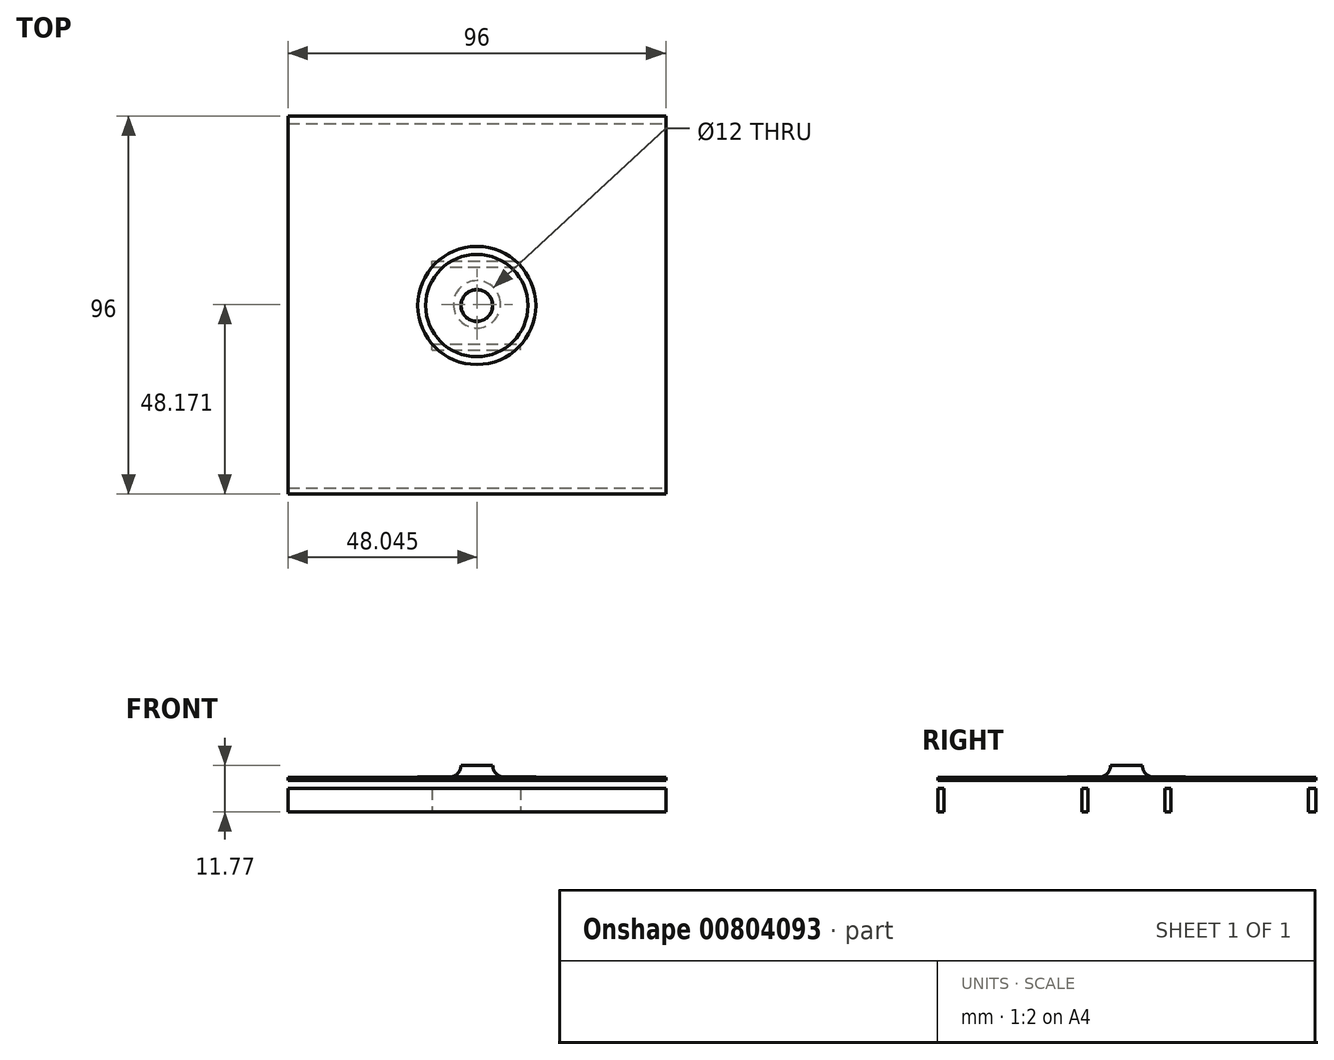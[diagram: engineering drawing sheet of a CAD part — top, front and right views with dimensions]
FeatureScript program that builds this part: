
annotation { "Feature Type Name" : "Feature", "Feature Type Description" : "" }
export const myFeature = defineFeature(function(context is Context, id is Id, definition is map)
    precondition{}
    {
        {
            var Q0;
            Q0=qCreatedBy(makeId("Top.planeOp"),FACE);
            var sketch = newSketch(context, id + "F0", { "sketchPlane" : qUnion([Q0])});
            skLineSegment(sketch, "E0.bottom", {"start": v(-47.87, 48.13) * mm, "end": v(48.13, 48.13) * mm});
            skLineSegment(sketch, "E0.top", {"start": v(-47.87, 46.17) * mm, "end": v(48.13, 46.17) * mm});
            skLineSegment(sketch, "E0.left", {"start": v(-47.87, 48.13) * mm, "end": v(-47.87, 46.17) * mm});
            skLineSegment(sketch, "E0.right", {"start": v(48.13, 48.13) * mm, "end": v(48.13, 46.17) * mm});
            skLineSegment(sketch, "E1.bottom", {"start": v(-47.87, 46.17) * mm, "end": v(-46.43, 46.17) * mm});
            skLineSegment(sketch, "E1.top", {"start": v(-47.87, -46.37) * mm, "end": v(-46.43, -46.37) * mm});
            skLineSegment(sketch, "E1.left", {"start": v(-47.87, 46.17) * mm, "end": v(-47.87, -46.37) * mm});
            skLineSegment(sketch, "E1.right", {"start": v(-46.43, 46.17) * mm, "end": v(-46.43, -46.37) * mm});
            skLineSegment(sketch, "E2.bottom", {"start": v(-47.87, -46.37) * mm, "end": v(48.13, -46.37) * mm});
            skLineSegment(sketch, "E2.top", {"start": v(-47.87, -47.87) * mm, "end": v(48.13, -47.87) * mm});
            skLineSegment(sketch, "E2.left", {"start": v(-47.87, -46.37) * mm, "end": v(-47.87, -47.87) * mm});
            skLineSegment(sketch, "E2.right", {"start": v(48.13, -46.37) * mm, "end": v(48.13, -47.87) * mm});
            skLineSegment(sketch, "E3.bottom", {"start": v(48.13, 46.17) * mm, "end": v(46.57, 46.17) * mm});
            skLineSegment(sketch, "E3.top", {"start": v(48.13, -46.37) * mm, "end": v(46.57, -46.37) * mm});
            skLineSegment(sketch, "E3.left", {"start": v(48.13, 46.17) * mm, "end": v(48.13, -46.37) * mm});
            skLineSegment(sketch, "E3.right", {"start": v(46.57, 46.17) * mm, "end": v(46.57, -46.37) * mm});
            skLineSegment(sketch, "E4.bottom", {"start": v(-11.25, -11.25) * mm, "end": v(11.25, -11.25) * mm});
            skLineSegment(sketch, "E4.top", {"start": v(-11.25, 11.25) * mm, "end": v(11.25, 11.25) * mm});
            skLineSegment(sketch, "E4.left", {"start": v(-11.25, -11.25) * mm, "end": v(-11.25, 11.25) * mm});
            skLineSegment(sketch, "E4.right", {"start": v(11.25, -11.25) * mm, "end": v(11.25, 11.25) * mm});
            skPoint(sketch, "E4.middle", {"position": v(0, 0) * mm});
            skLineSegment(sketch, "E5.bottom", {"start": v(-11.25, 46.17) * mm, "end": v(-12.75, 46.17) * mm});
            skLineSegment(sketch, "E5.top", {"start": v(-11.25, -46.37) * mm, "end": v(-12.75, -46.37) * mm});
            skLineSegment(sketch, "E5.left", {"start": v(-11.25, 46.17) * mm, "end": v(-11.25, -46.37) * mm});
            skLineSegment(sketch, "E5.right", {"start": v(-12.75, 46.17) * mm, "end": v(-12.75, -46.37) * mm});
            skLineSegment(sketch, "E6.bottom", {"start": v(-0.75, 11.25) * mm, "end": v(0.75, 11.25) * mm});
            skLineSegment(sketch, "E6.top", {"start": v(-0.75, 46.17) * mm, "end": v(0.75, 46.17) * mm});
            skLineSegment(sketch, "E6.left", {"start": v(-0.75, 11.25) * mm, "end": v(-0.75, 46.17) * mm});
            skLineSegment(sketch, "E6.right", {"start": v(0.75, 11.25) * mm, "end": v(0.75, 46.17) * mm});
            skLineSegment(sketch, "E7", {"start": v(0, 0) * mm, "end": v(0, 0) * mm, "construction": true});
            skLineSegment(sketch, "E8.top", {"start": v(-11.25, 9.75) * mm, "end": v(11.25, 9.75) * mm});
            skLineSegment(sketch, "E8.left", {"start": v(-11.25, 11.25) * mm, "end": v(-11.25, 9.75) * mm});
            skLineSegment(sketch, "E8.right", {"start": v(11.25, 11.25) * mm, "end": v(11.25, 9.75) * mm});
            skLineSegment(sketch, "E9.top", {"start": v(-11.25, -9.75) * mm, "end": v(11.25, -9.75) * mm});
            skLineSegment(sketch, "E9.left", {"start": v(-11.25, -11.25) * mm, "end": v(-11.25, -9.75) * mm});
            skLineSegment(sketch, "E9.right", {"start": v(11.25, -11.25) * mm, "end": v(11.25, -9.75) * mm});
            skLineSegment(sketch, "E10.bottom", {"start": v(-0.77, -11.25) * mm, "end": v(0.73, -11.25) * mm});
            skLineSegment(sketch, "E10.top", {"start": v(-0.77, -46.37) * mm, "end": v(0.73, -46.37) * mm});
            skLineSegment(sketch, "E10.left", {"start": v(-0.77, -11.25) * mm, "end": v(-0.77, -46.37) * mm});
            skLineSegment(sketch, "E10.right", {"start": v(0.73, -11.25) * mm, "end": v(0.73, -46.37) * mm});
            skLineSegment(sketch, "E11.bottom", {"start": v(11.25, -46.37) * mm, "end": v(12.75, -46.37) * mm});
            skLineSegment(sketch, "E11.top", {"start": v(11.25, 46.17) * mm, "end": v(12.75, 46.17) * mm});
            skLineSegment(sketch, "E11.left", {"start": v(11.25, -46.37) * mm, "end": v(11.25, 46.17) * mm});
            skLineSegment(sketch, "E11.right", {"start": v(12.75, -46.37) * mm, "end": v(12.75, 46.17) * mm});
            skLineSegment(sketch, "E12.bottom", {"start": v(-22.73, -46.37) * mm, "end": v(-24.23, -46.37) * mm});
            skLineSegment(sketch, "E12.top", {"start": v(-22.73, 46.17) * mm, "end": v(-24.23, 46.17) * mm});
            skLineSegment(sketch, "E12.left", {"start": v(-22.73, -46.37) * mm, "end": v(-22.73, 46.17) * mm});
            skLineSegment(sketch, "E12.right", {"start": v(-24.23, -46.37) * mm, "end": v(-24.23, 46.17) * mm});
            skLineSegment(sketch, "E13.bottom", {"start": v(-34.71, -46.37) * mm, "end": v(-36.21, -46.37) * mm});
            skLineSegment(sketch, "E13.top", {"start": v(-34.71, 46.17) * mm, "end": v(-36.21, 46.17) * mm});
            skLineSegment(sketch, "E13.left", {"start": v(-34.71, -46.37) * mm, "end": v(-34.71, 46.17) * mm});
            skLineSegment(sketch, "E13.right", {"start": v(-36.21, -46.37) * mm, "end": v(-36.21, 46.17) * mm});
            skLineSegment(sketch, "E14.bottom", {"start": v(23.23, -46.37) * mm, "end": v(24.73, -46.37) * mm});
            skLineSegment(sketch, "E14.top", {"start": v(23.23, 46.17) * mm, "end": v(24.73, 46.17) * mm});
            skLineSegment(sketch, "E14.left", {"start": v(23.23, -46.37) * mm, "end": v(23.23, 46.17) * mm});
            skLineSegment(sketch, "E14.right", {"start": v(24.73, -46.37) * mm, "end": v(24.73, 46.17) * mm});
            skLineSegment(sketch, "E15.bottom", {"start": v(35.22, 46.17) * mm, "end": v(36.72, 46.17) * mm});
            skLineSegment(sketch, "E15.top", {"start": v(35.22, -46.37) * mm, "end": v(36.72, -46.37) * mm});
            skLineSegment(sketch, "E15.left", {"start": v(35.22, 46.17) * mm, "end": v(35.22, -46.37) * mm});
            skLineSegment(sketch, "E15.right", {"start": v(36.72, 46.17) * mm, "end": v(36.72, -46.37) * mm});
            skSolve(sketch);
        }
        {
            var Q0;
            Q0=makeQuery(id+"F0.imprint","IMPRINT",FACE,{"disambiguationData":[TD([[makeQuery(id+"F0.imprint","IMPRINT",EDGE,{"derivedFrom":sQuery(id+"F0.wireOp",EDGE,"E13.bottom")}),-1.0]])]});
            var Q1;
            Q1=makeQuery(id+"F0.imprint","IMPRINT",FACE,{"disambiguationData":[TD([[makeQuery(id+"F0.imprint","IMPRINT",EDGE,{"derivedFrom":sQuery(id+"F0.wireOp",EDGE,"E1.bottom")}),-1.0]])]});
            var Q2;
            Q2=makeQuery(id+"F0.imprint","IMPRINT",FACE,{"disambiguationData":[TD([[makeQuery(id+"F0.imprint","IMPRINT",EDGE,{"derivedFrom":sQuery(id+"F0.wireOp",EDGE,"E12.bottom")}),-1.0]])]});
            var Q3;
            {var subQ3=sQuery(id+"F0.wireOp",EDGE,"E5.bottom");Q3=makeQuery(id+"F0.imprint","IMPRINT",FACE,{"disambiguationData":[TD([[makeQuery(id+"F0.imprint","IMPRINT",EDGE,{"derivedFrom":subQ3}),1.0]])]});}
            var Q4;
            {var subQ3=sQuery(id+"F0.wireOp",EDGE,"E11.bottom");Q4=makeQuery(id+"F0.imprint","IMPRINT",FACE,{"disambiguationData":[TD([[makeQuery(id+"F0.imprint","IMPRINT",EDGE,{"derivedFrom":subQ3}),1.0]])]});}
            var Q5;
            Q5=makeQuery(id+"F0.imprint","IMPRINT",FACE,{"disambiguationData":[TD([[makeQuery(id+"F0.imprint","IMPRINT",EDGE,{"derivedFrom":sQuery(id+"F0.wireOp",EDGE,"E14.bottom")}),1.0]])]});
            var Q6;
            Q6=makeQuery(id+"F0.imprint","IMPRINT",FACE,{"disambiguationData":[TD([[makeQuery(id+"F0.imprint","IMPRINT",EDGE,{"derivedFrom":sQuery(id+"F0.wireOp",EDGE,"E15.bottom")}),-1.0]])]});
            var Q7;
            Q7=makeQuery(id+"F0.imprint","IMPRINT",FACE,{"disambiguationData":[TD([[makeQuery(id+"F0.imprint","IMPRINT",EDGE,{"derivedFrom":sQuery(id+"F0.wireOp",EDGE,"E3.bottom")}),1.0]])]});
            var Q8;
            Q8=makeQuery(id+"F0.imprint","IMPRINT",FACE,{"disambiguationData":[TD([[makeQuery(id+"F0.imprint","IMPRINT",EDGE,{"derivedFrom":sQuery(id+"F0.wireOp",EDGE,"E10.bottom")}),-1.0]])]});
            var Q9;
            Q9=makeQuery(id+"F0.imprint","IMPRINT",FACE,{"disambiguationData":[TD([[makeQuery(id+"F0.imprint","IMPRINT",EDGE,{"derivedFrom":sQuery(id+"F0.wireOp",EDGE,"E6.top")}),-1.0]])]});
            var Q10;
            {var subQ0=sQuery(id+"F0.wireOp",EDGE,"E8.top");Q10=makeQuery(id+"F0.imprint","IMPRINT",FACE,{"disambiguationData":[TD([[makeQuery(id+"F0.imprint","IMPRINT",EDGE,{"derivedFrom":subQ0}),1.0]])]});}
            var Q11;
            {var subQ1=sQuery(id+"F0.wireOp",EDGE,"E9.top");Q11=makeQuery(id+"F0.imprint","IMPRINT",FACE,{"disambiguationData":[TD([[makeQuery(id+"F0.imprint","IMPRINT",EDGE,{"derivedFrom":subQ1}),-1.0]])]});}
            var Q12;
            Q12=makeQuery(id+"F0.imprint","IMPRINT",FACE,{"disambiguationData":[TD([[makeQuery(id+"F0.imprint","IMPRINT",EDGE,{"derivedFrom":sQuery(id+"F0.wireOp",EDGE,"E2.top")}),1.0]])]});
            var Q13;
            Q13=makeQuery(id+"F0.imprint","IMPRINT",FACE,{"disambiguationData":[TD([[makeQuery(id+"F0.imprint","IMPRINT",EDGE,{"derivedFrom":sQuery(id+"F0.wireOp",EDGE,"E0.bottom")}),-1.0]])]});
            extrude(context, id + "F1", {"entities" : qUnion([Q0, Q1, Q2, Q3, Q4, Q5, Q6, Q7, Q8, Q9, Q10, Q11, Q12, Q13]), "depth" : 6 * mm, "offsetDistance" : 25 * mm});
        }
        {
            var Q0;
            Q0=makeQuery(id+"F1.opExtrude","CAP_FACE",FACE,{"disambiguationData":[OSD([sQuery(id+"F0.wireOp",EDGE,"E0.bottom"),sQuery(id+"F0.wireOp",EDGE,"E0.top"),sQuery(id+"F0.wireOp",EDGE,"E0.left"),sQuery(id+"F0.wireOp",EDGE,"E0.right"),sQuery(id+"F0.wireOp",EDGE,"E1.left"),sQuery(id+"F0.wireOp",EDGE,"E1.right"),sQuery(id+"F0.wireOp",EDGE,"E2.bottom"),sQuery(id+"F0.wireOp",EDGE,"E2.top"),sQuery(id+"F0.wireOp",EDGE,"E2.left"),sQuery(id+"F0.wireOp",EDGE,"E2.right"),sQuery(id+"F0.wireOp",EDGE,"E3.top"),sQuery(id+"F0.wireOp",EDGE,"E3.left"),sQuery(id+"F0.wireOp",EDGE,"E3.right"),sQuery(id+"F0.wireOp",EDGE,"E5.left"),sQuery(id+"F0.wireOp",EDGE,"E5.right"),sQuery(id+"F0.wireOp",EDGE,"E6.left"),sQuery(id+"F0.wireOp",EDGE,"E6.right"),sQuery(id+"F0.wireOp",EDGE,"E4.top"),sQuery(id+"F0.wireOp",EDGE,"E8.top"),sQuery(id+"F0.wireOp",EDGE,"E4.bottom"),sQuery(id+"F0.wireOp",EDGE,"E9.top"),sQuery(id+"F0.wireOp",EDGE,"E10.left"),sQuery(id+"F0.wireOp",EDGE,"E10.right"),sQuery(id+"F0.wireOp",EDGE,"E11.left"),sQuery(id+"F0.wireOp",EDGE,"E11.right"),sQuery(id+"F0.wireOp",EDGE,"E12.left"),sQuery(id+"F0.wireOp",EDGE,"E12.right"),sQuery(id+"F0.wireOp",EDGE,"E13.left"),sQuery(id+"F0.wireOp",EDGE,"E13.right"),sQuery(id+"F0.wireOp",EDGE,"E14.left"),sQuery(id+"F0.wireOp",EDGE,"E14.right"),sQuery(id+"F0.wireOp",EDGE,"E15.left"),sQuery(id+"F0.wireOp",EDGE,"E15.right")])],"isStart":false});
            var sketch = newSketch(context, id + "F2", { "sketchPlane" : qUnion([Q0])});
            skLineSegment(sketch, "E16.bottom", {"start": v(-47.87, 48.13) * mm, "end": v(48.13, 48.13) * mm});
            skLineSegment(sketch, "E16.top", {"start": v(-47.87, -47.87) * mm, "end": v(48.13, -47.87) * mm});
            skLineSegment(sketch, "E16.left", {"start": v(-47.87, 48.13) * mm, "end": v(-47.87, -47.87) * mm});
            skLineSegment(sketch, "E16.right", {"start": v(48.13, 48.13) * mm, "end": v(48.13, -47.87) * mm});
            skSolve(sketch);
        }
        {
            var Q0;
            {var subQ42=sQuery(id+"F2.wireOp",EDGE,"E16.bottom");Q0=makeQuery(id+"F2.imprint","IMPRINT",FACE,{"disambiguationData":[TD([[makeQuery(id+"F2.imprint","IMPRINT",EDGE,{"derivedFrom":subQ42}),-1.0]])]});}
            cPlane(context, id + "F3", {"entities" : qUnion([Q0]), "cplaneType" : CPlaneType.OFFSET, "offset" : 2 * mm, "width" : 150 * mm, "height" : 150 * mm});
        }
        {
            var Q0;
            Q0=qCreatedBy(id+"F3.planeOp",FACE);
            var sketch = newSketch(context, id + "F4", { "sketchPlane" : qUnion([Q0])});
            skLineSegment(sketch, "E17.bottom", {"start": v(48.13, -47.87) * mm, "end": v(-47.87, -47.87) * mm});
            skLineSegment(sketch, "E17.top", {"start": v(48.13, 48.13) * mm, "end": v(-47.87, 48.13) * mm});
            skLineSegment(sketch, "E17.left", {"start": v(48.13, -47.87) * mm, "end": v(48.13, 48.13) * mm});
            skLineSegment(sketch, "E17.right", {"start": v(-47.87, -47.87) * mm, "end": v(-47.87, 48.13) * mm});
            skPoint(sketch, "E17.middle", {"position": v(0.13, 0.13) * mm});
            skSolve(sketch);
        }
        {
            var Q0;
            Q0 = qSketchRegion(id + "F4", true);
            extrude(context, id + "F5", {"entities" : qUnion([Q0]), "depth" : .75 * mm, "offsetDistance" : 25 * mm});
        }
        {
            var Q0;
            Q0=makeQuery(id+"F5.opExtrude","CAP_FACE",FACE,{"disambiguationData":[OSD([sQuery(id+"F4.wireOp",EDGE,"E17.bottom"),sQuery(id+"F4.wireOp",EDGE,"E17.top"),sQuery(id+"F4.wireOp",EDGE,"E17.left"),sQuery(id+"F4.wireOp",EDGE,"E17.right")])],"isStart":false});
            var sketch = newSketch(context, id + "F6", { "sketchPlane" : qUnion([Q0])});
            skLineSegment(sketch, "E18", {"start": v(-47.87, 0.13) * mm, "end": v(48.13, 0.13) * mm});
            skLineSegment(sketch, "E19", {"start": v(0.13, 48.13) * mm, "end": v(0.13, -47.87) * mm});
            skSolve(sketch);
        }
        {
            var Q0;
            {var subQ0=sQuery(id+"F6.wireOp",EDGE,"E18");var subQ1=makeQuery(id+"F5.opExtrude","CAP_EDGE",EDGE,{"disambiguationData":[OSD([sQuery(id+"F4.wireOp",EDGE,"E17.right")])],"isStart":false});var subQ2=makeQuery(id+"F6.imprint","INTERSECT",VERTEX,{"derivedFrom":[subQ1,subQ0]});Q0=makeQuery(id+"F6.imprint","IMPRINT",FACE,{"disambiguationData":[TD([[makeQuery(id+"F6.imprint","IMPRINT",EDGE,{"disambiguationData":[TD([[subQ2,-1.0]])],"derivedFrom":subQ0}),1.0]])]});}
            var sketch = newSketch(context, id + "F7", { "sketchPlane" : qUnion([Q0])});
            skPoint(sketch, "E20", {"position": v(0.17, 0.3) * mm});
            skSolve(sketch);
        }
        {
            var Q0;
            Q0=sQuery(id+"F7.wireOp",VERTEX,"E20");
            var Q1;
            Q1=makeQuery(id+"F5.opExtrude","SWEPT_BODY",BODY,{"disambiguationData":[OSD([sQuery(id+"F4.wireOp",EDGE,"E17.bottom"),sQuery(id+"F4.wireOp",EDGE,"E17.top"),sQuery(id+"F4.wireOp",EDGE,"E17.left"),sQuery(id+"F4.wireOp",EDGE,"E17.right")])]});
            hole(context, id + "F8", {"style" : HoleStyle.SIMPLE, "endStyle" : HoleEndStyle.THROUGH, "holeDiameter" : 12 * mm, "majorDiameter" : 5 * mm, "isTappedThrough" : true, "tappedDepth" : 12 * mm, "tapClearance" : 3, "locations" : qUnion([Q0]), "scope" : qUnion([Q1])});
        }
        {
            var Q0;
            Q0=qCreatedBy(makeId("Front.planeOp"),FACE);
            var sketch = newSketch(context, id + "F9", { "sketchPlane" : qUnion([Q0])});
            skLineSegment(sketch, "E21", {"start": v(0.13, 8.79) * mm, "end": v(0.13, 14.07) * mm, "construction": true});
            skPoint(sketch, "E22", {"position": v(0.13, 11.75) * mm});
            skArc(sketch, "E23", {"start": v(4.13, 11.77) * mm, "mid": v(5, 9.65) * mm, "end": v(7.13, 8.77) * mm});
            skLineSegment(sketch, "E24", {"start": v(7.13, 8.77) * mm, "end": v(15.13, 8.78) * mm});
            skArc(sketch, "E25", {"start": v(7.13, 8.82) * mm, "mid": v(5.04, 9.68) * mm, "end": v(4.18, 11.77) * mm});
            skLineSegment(sketch, "E26", {"start": v(4.13, 11.77) * mm, "end": v(4.18, 11.77) * mm});
            skLineSegment(sketch, "E27", {"start": v(7.13, 8.82) * mm, "end": v(15.13, 8.83) * mm});
            skLineSegment(sketch, "E28", {"start": v(15.13, 8.83) * mm, "end": v(15.13, 8.78) * mm});
            skSolve(sketch);
        }
        {
            var Q0;
            Q0=makeQuery(id+"F9.imprint","IMPRINT",FACE,{"disambiguationData":[TD([[makeQuery(id+"F9.imprint","IMPRINT",EDGE,{"derivedFrom":sQuery(id+"F9.wireOp",EDGE,"E23")}),1.0]])]});
            var Q1;
            Q1=sQuery(id+"F9.wireOp",EDGE,"E21");
            revolve(context, id + "F10", {"surfaceOperationType" : NewSurfaceOperationType.NEW, "entities" : qUnion([Q0]), "axis" : qUnion([Q1]), "revolveType" : RevolveType.FULL});
        }
        {
            var Q0;
            Q0=qCreatedBy(makeId("Front.planeOp"),FACE);
            var sketch = newSketch(context, id + "F11", { "sketchPlane" : qUnion([Q0])});
            skLineSegment(sketch, "E29.bottom", {"start": v(15.13, 8.83) * mm, "end": v(13.13, 8.83) * mm});
            skLineSegment(sketch, "E29.top", {"start": v(15.13, 8.9) * mm, "end": v(13.13, 8.9) * mm});
            skLineSegment(sketch, "E29.left", {"start": v(15.13, 8.83) * mm, "end": v(15.13, 8.9) * mm});
            skLineSegment(sketch, "E29.right", {"start": v(13.13, 8.83) * mm, "end": v(13.13, 8.9) * mm});
            skSolve(sketch);
        }
        {
            var Q0;
            Q0=makeQuery(id+"F11.imprint","IMPRINT",FACE,{"disambiguationData":[TD([[makeQuery(id+"F11.imprint","IMPRINT",EDGE,{"derivedFrom":sQuery(id+"F11.wireOp",EDGE,"E29.bottom")}),-1.0]])]});
            var Q1;
            Q1=sQuery(id+"F9.wireOp",EDGE,"E21");
            revolve(context, id + "F12", {"surfaceOperationType" : NewSurfaceOperationType.NEW, "entities" : qUnion([Q0]), "axis" : qUnion([Q1]), "revolveType" : RevolveType.FULL});
        }
        {
            var Q0;
            Q0=makeQuery(id+"F12.opRevolve","SWEPT_EDGE",EDGE,{"disambiguationData":[OSD([sQuery(id+"F11.wireOp",EDGE,"E29.top"),sQuery(id+"F11.wireOp",EDGE,"E29.left")])]});
            fillet(context, id + "F13", {"entities" : qUnion([Q0]), "radius" : .5 * mm, "tangentPropagation" : true, "allowEdgeOverflow" : false});
        }
        {
            var Q0;
            Q0=makeQuery(id+"F12.opRevolve","SWEPT_EDGE",EDGE,{"disambiguationData":[OSD([sQuery(id+"F11.wireOp",EDGE,"E29.top"),sQuery(id+"F11.wireOp",EDGE,"E29.right")])]});
            fillet(context, id + "F14", {"entities" : qUnion([Q0]), "radius" : .5 * mm, "tangentPropagation" : true, "allowEdgeOverflow" : false});
        }
    });
